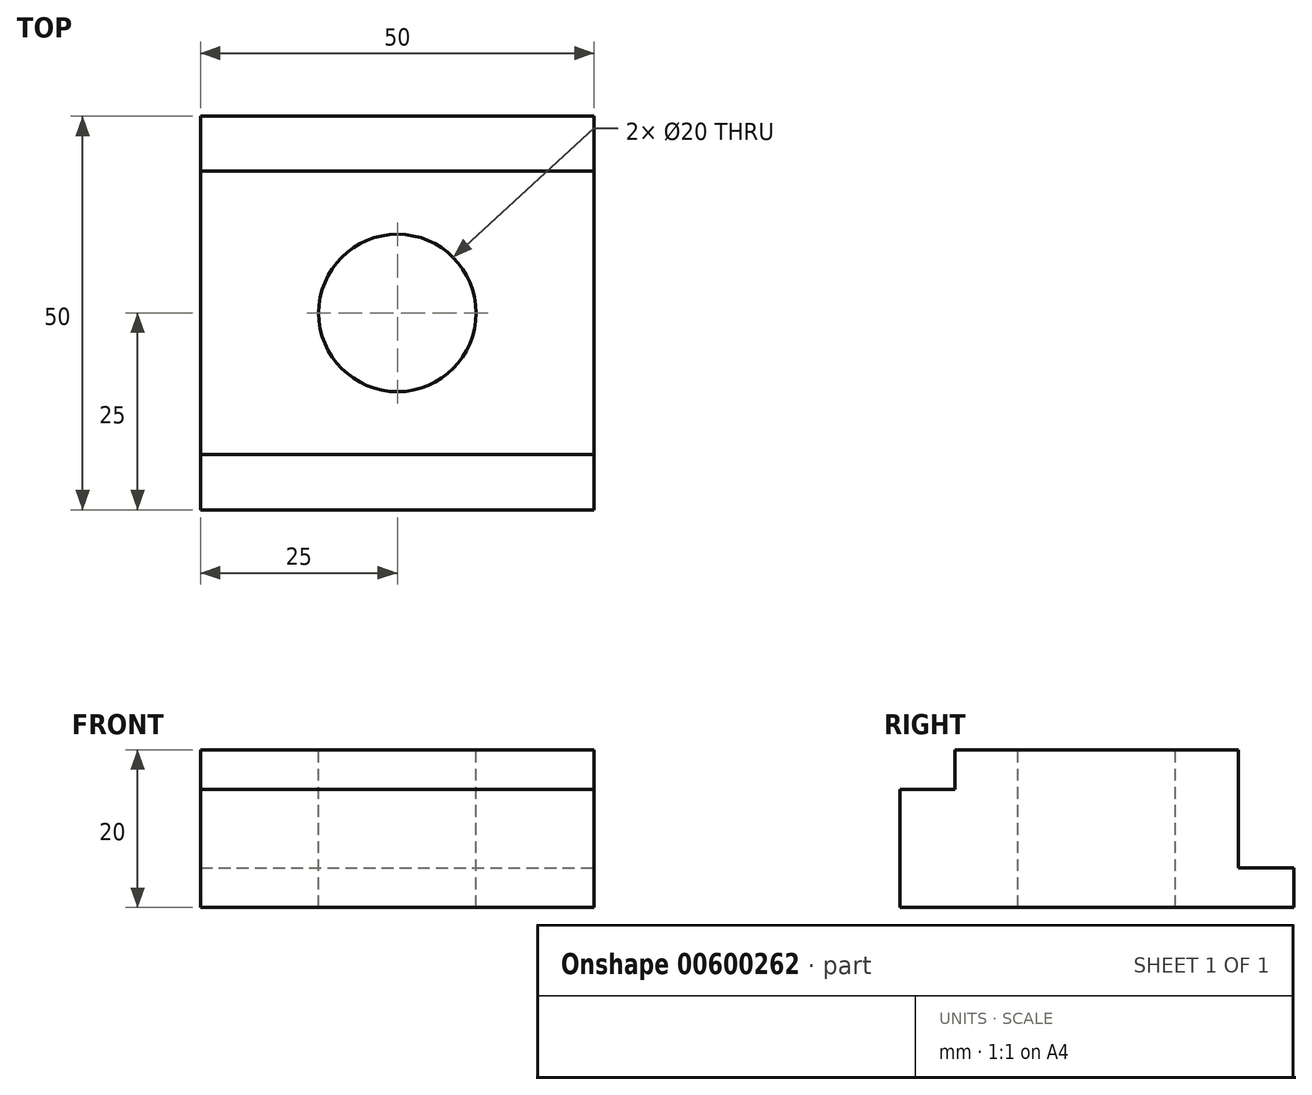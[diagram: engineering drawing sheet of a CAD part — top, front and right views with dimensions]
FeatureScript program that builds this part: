
annotation { "Feature Type Name" : "Feature", "Feature Type Description" : "" }
export const myFeature = defineFeature(function(context is Context, id is Id, definition is map)
    precondition{}
    {
        {
            var Q0;
            Q0=qCreatedBy(makeId("Right.planeOp"),FACE);
            var sketch = newSketch(context, id + "F0", { "sketchPlane" : qUnion([Q0])});
            skLineSegment(sketch, "E0.bottom", {"start": v(0, 0) * mm, "end": v(50, 0) * mm});
            skLineSegment(sketch, "E0.top", {"start": v(0, 20) * mm, "end": v(50, 20) * mm});
            skLineSegment(sketch, "E0.left", {"start": v(0, 0) * mm, "end": v(0, 20) * mm});
            skLineSegment(sketch, "E0.right", {"start": v(50, 0) * mm, "end": v(50, 20) * mm});
            skSolve(sketch);
        }
        {
            var Q0;
            Q0 = qSketchRegion(id + "F0", true);
            extrude(context, id + "F1", {"entities" : qUnion([Q0]), "depth" : 50 * mm, "offsetDistance" : 25 * mm});
        }
        {
            var Q0;
            Q0=makeQuery(id+"F1.opExtrude","CAP_FACE",FACE,{"disambiguationData":[OSD([sQuery(id+"F0.wireOp",EDGE,"E0.bottom"),sQuery(id+"F0.wireOp",EDGE,"E0.top"),sQuery(id+"F0.wireOp",EDGE,"E0.left"),sQuery(id+"F0.wireOp",EDGE,"E0.right")])],"isStart":false});
            var sketch = newSketch(context, id + "F2", { "sketchPlane" : qUnion([Q0])});
            skLineSegment(sketch, "E1.bottom", {"start": v(0, 20) * mm, "end": v(7, 20) * mm});
            skLineSegment(sketch, "E1.top", {"start": v(0, 15) * mm, "end": v(7, 15) * mm});
            skLineSegment(sketch, "E1.left", {"start": v(0, 20) * mm, "end": v(0, 15) * mm});
            skLineSegment(sketch, "E1.right", {"start": v(7, 20) * mm, "end": v(7, 15) * mm});
            skLineSegment(sketch, "E2.bottom", {"start": v(50, 20) * mm, "end": v(43, 20) * mm});
            skLineSegment(sketch, "E2.top", {"start": v(50, 5) * mm, "end": v(43, 5) * mm});
            skLineSegment(sketch, "E2.left", {"start": v(50, 20) * mm, "end": v(50, 5) * mm});
            skLineSegment(sketch, "E2.right", {"start": v(43, 20) * mm, "end": v(43, 5) * mm});
            skSolve(sketch);
        }
        {
            var Q0;
            Q0=makeQuery(id+"F2.imprint","IMPRINT",FACE,{"disambiguationData":[TD([[makeQuery(id+"F2.imprint","IMPRINT",EDGE,{"derivedFrom":sQuery(id+"F2.wireOp",EDGE,"E1.bottom")}),-1.0]])]});
            var Q1;
            Q1=makeQuery(id+"F2.imprint","IMPRINT",FACE,{"disambiguationData":[TD([[makeQuery(id+"F2.imprint","IMPRINT",EDGE,{"derivedFrom":sQuery(id+"F2.wireOp",EDGE,"E2.bottom")}),-1.0]])]});
            extrude(context, id + "F3", {"entities" : qUnion([Q0, Q1]), "operationType" : NewBodyOperationType.REMOVE, "oppositeDirection" : true, "depth" : 50 * mm, "offsetDistance" : 25 * mm});
        }
        {
            var Q0;
            Q0=makeQuery(id+"F1.opExtrude","SWEPT_FACE",FACE,{"disambiguationData":[OSD([sQuery(id+"F0.wireOp",EDGE,"E0.top")])]});
            var sketch = newSketch(context, id + "F4", { "sketchPlane" : qUnion([Q0])});
            skCircle(sketch, "E3", {"center": v(25, 25) * mm, "radius": 10 * mm});
            skSolve(sketch);
        }
        {
            var Q0;
            Q0 = qSketchRegion(id + "F4", true);
            extrude(context, id + "F5", {"entities" : qUnion([Q0]), "operationType" : NewBodyOperationType.REMOVE, "oppositeDirection" : true, "depth" : 20 * mm, "offsetDistance" : 25 * mm});
        }
    });
